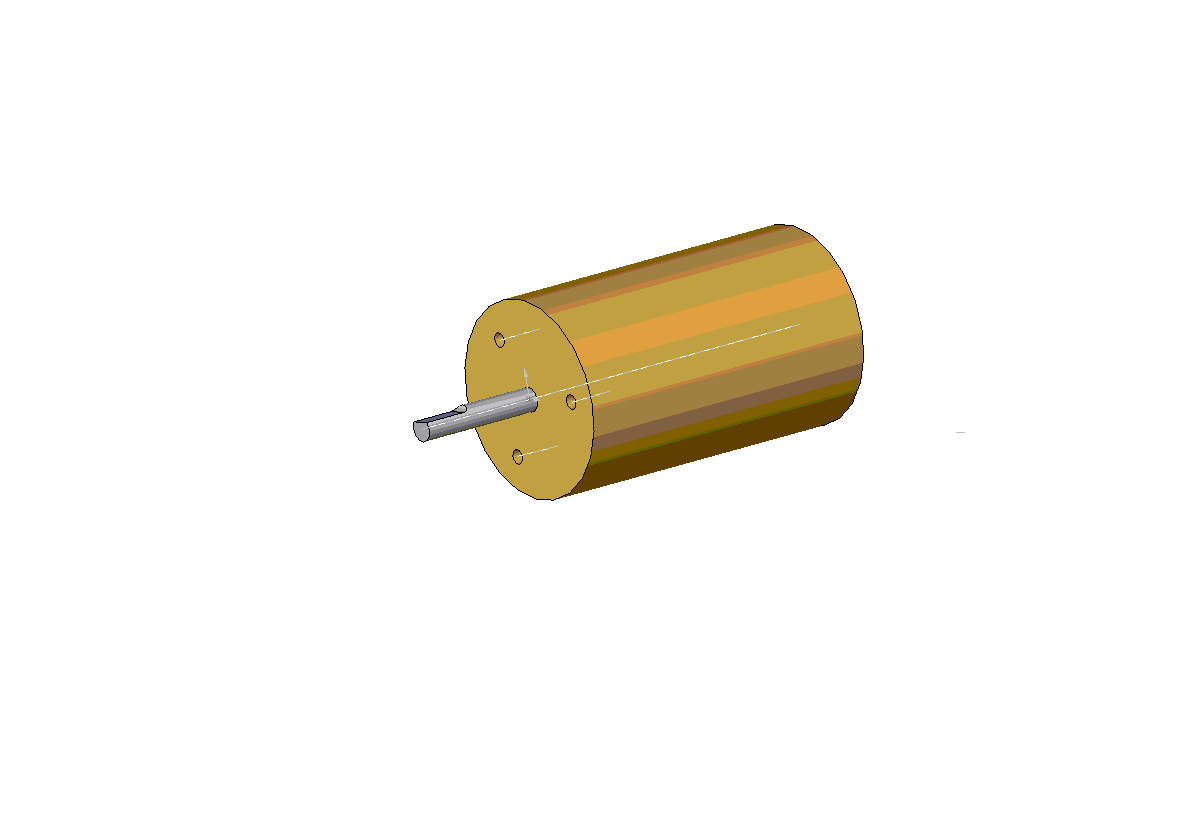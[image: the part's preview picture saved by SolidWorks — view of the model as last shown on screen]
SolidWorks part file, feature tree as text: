
SOLIDWORKS PART (.sldprt)
format: sldprt  version: not decoded by parser v0  size: 135,680 bytes
history: native  units: mm
features: sketch x5, extrude x2, material x1, cut_extrude x1, hole x1, pattern_circular x1 (+11 scaffold rows collapsed)
feature tree (22):
  scaffold x11  (default folders/planes/origin — collapsed)
  material  "Material <not specified>"
  sketch  "Sketch1"  dims[body_diameter=38.1mm]
  extrude  "body"  Depth=63.5mm body_length=63.5mm
  sketch  "Sketch2"  dims[shaft_diameter=4.7625mm]
  extrude  "shaft"  Depth=25.4mm shaft_length=25.4mm
  sketch  "Sketch3"  dims[D2=1.5875mm D1=10.16mm D3=1.016mm]
  cut_extrude  "shaft-flat"  [1 undecoded]
  hole  "mounting_hole"  Diameter=2.2606mm Depth=8.8646mm
  sketch  "Sketch5"  dims[bolt_circle_radius=12.7mm]
  sketch  "Sketch4"  dims[hole-wizard template sketch: 29 standard entries collapsed; hole parameters kept: c8.Tap Drill Depth=8.8646mm c8.Thread Dia.=2.8448mm c8.Thread Depth=5.6896mm c8.D5=~14.816244mm c8.Drill Angle=118.0deg]
  pattern_circular  "CirPattern1"  Count=3 Angle=360deg
decode coverage: 9 of 10 modeling features carry decoded parameters
note: ~ marks probable driven/reference dimensions
note: 1 parameter value undecoded
note: suppression state not decoded; provenance and decode notes live in map.json
